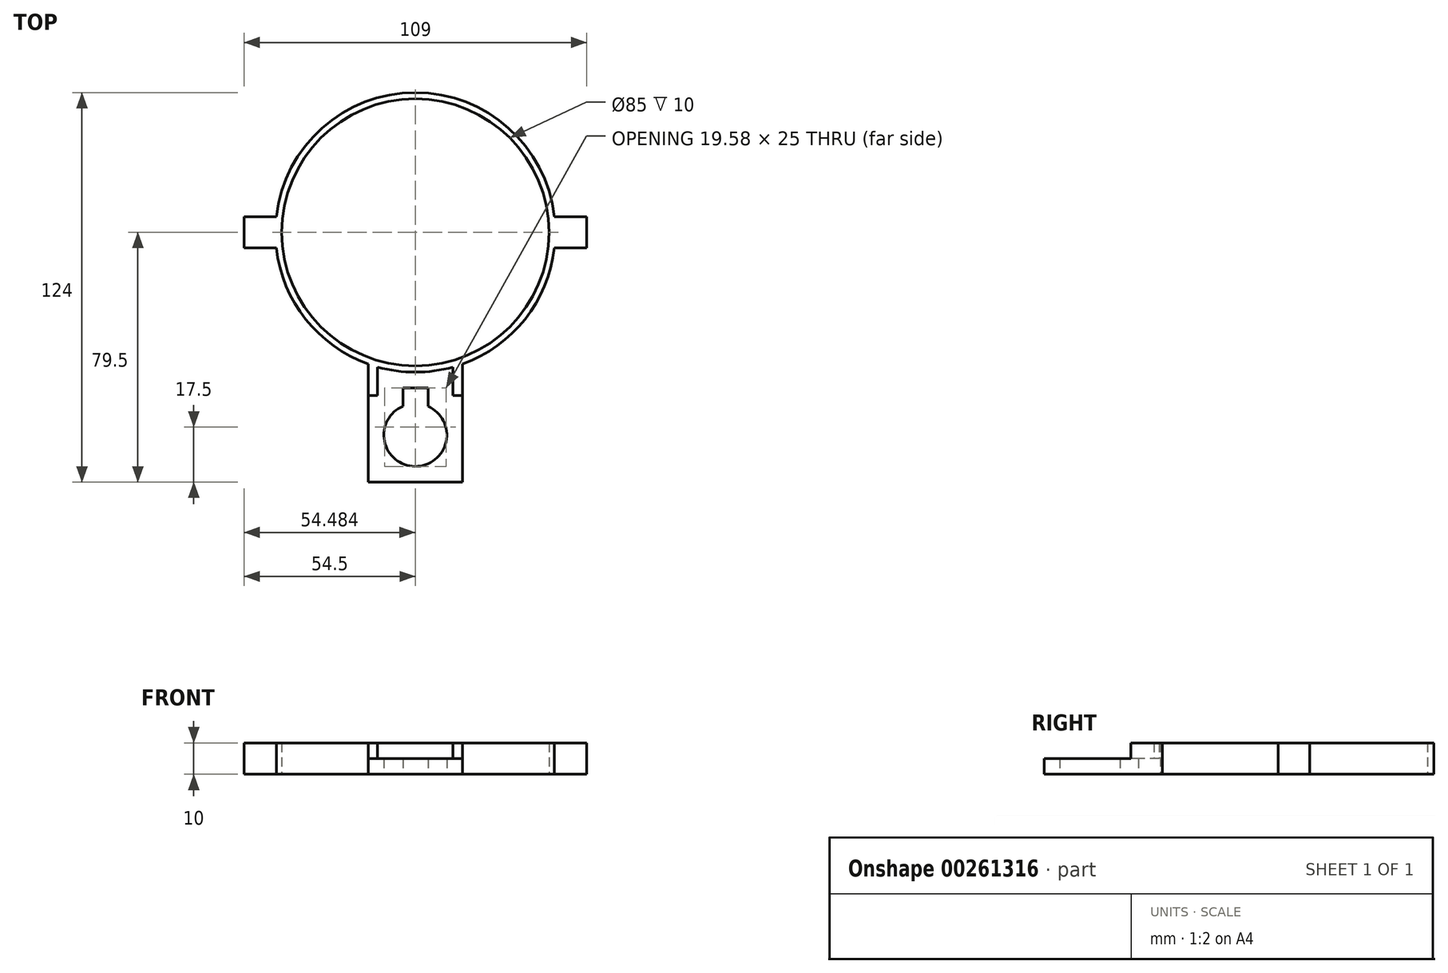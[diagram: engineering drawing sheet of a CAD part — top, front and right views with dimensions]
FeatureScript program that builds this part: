
annotation { "Feature Type Name" : "Feature", "Feature Type Description" : "" }
export const myFeature = defineFeature(function(context is Context, id is Id, definition is map)
    precondition{}
    {
        {
            var Q0;
            Q0=qCreatedBy(makeId("Top.planeOp"),FACE);
            var sketch = newSketch(context, id + "F0", { "sketchPlane" : qUnion([Q0])});
            skCircle(sketch, "E0", {"center": v(0, 0) * mm, "radius": 42.5 * mm});
            skCircle(sketch, "E1", {"center": v(0, 0) * mm, "radius": 44.5 * mm});
            skLineSegment(sketch, "E2.bottom", {"start": v(-54.5, 5) * mm, "end": v(-42.5, 5) * mm});
            skLineSegment(sketch, "E2.top", {"start": v(-54.5, -5) * mm, "end": v(-42.5, -5) * mm});
            skLineSegment(sketch, "E2.left", {"start": v(-54.5, 5) * mm, "end": v(-54.5, -5) * mm});
            skLineSegment(sketch, "E2.right", {"start": v(-42.5, 5) * mm, "end": v(-42.5, -5) * mm});
            skLineSegment(sketch, "E3.MirrorCS", {"start": v(54.5, 5) * mm, "end": v(54.5, -5) * mm});
            skLineSegment(sketch, "E4.MirrorCS", {"start": v(54.5, -5) * mm, "end": v(42.5, -5) * mm});
            skLineSegment(sketch, "E5.MirrorCS", {"start": v(54.5, 5) * mm, "end": v(42.5, 5) * mm});
            skLineSegment(sketch, "E6.MirrorCS", {"start": v(42.5, 5) * mm, "end": v(42.5, -5) * mm});
            skLineSegment(sketch, "E7.top", {"start": v(-15, -79.5) * mm, "end": v(15, -79.5) * mm});
            skLineSegment(sketch, "E7.left", {"start": v(-15, -41.9) * mm, "end": v(-15, -79.5) * mm});
            skLineSegment(sketch, "E7.right", {"start": v(15, -41.9) * mm, "end": v(15, -79.5) * mm});
            skCircle(sketch, "E8", {"center": v(0, -64.5) * mm, "radius": 10 * mm});
            skLineSegment(sketch, "E9.bottom", {"start": v(-3.93, -49.5) * mm, "end": v(4.07, -49.5) * mm});
            skLineSegment(sketch, "E9.top", {"start": v(-3.93, -64.5) * mm, "end": v(4.07, -64.5) * mm});
            skLineSegment(sketch, "E9.left", {"start": v(-3.93, -49.5) * mm, "end": v(-3.93, -64.5) * mm});
            skLineSegment(sketch, "E9.right", {"start": v(4.07, -49.5) * mm, "end": v(4.07, -64.5) * mm});
            skLineSegment(sketch, "E10.bottom", {"start": v(-15, -41.9) * mm, "end": v(-12, -41.9) * mm});
            skLineSegment(sketch, "E10.top", {"start": v(-15, -51.9) * mm, "end": v(-12, -51.9) * mm});
            skLineSegment(sketch, "E10.left", {"start": v(-15, -41.9) * mm, "end": v(-15, -51.9) * mm});
            skLineSegment(sketch, "E10.right", {"start": v(-12, -41.9) * mm, "end": v(-12, -51.9) * mm});
            skLineSegment(sketch, "E11.MirrorCS", {"start": v(15, -41.9) * mm, "end": v(12, -41.9) * mm});
            skLineSegment(sketch, "E12.MirrorCS", {"start": v(15, -51.9) * mm, "end": v(12, -51.9) * mm});
            skLineSegment(sketch, "E13.MirrorCS", {"start": v(15, -41.9) * mm, "end": v(15, -51.9) * mm});
            skLineSegment(sketch, "E14.MirrorCS", {"start": v(12, -41.9) * mm, "end": v(12, -51.9) * mm});
            skSolve(sketch);
        }
        {
            var Q0;
            {var subQ5=sQuery(id+"F0.wireOp",EDGE,"E2.left");Q0=makeQuery(id+"F0.imprint","IMPRINT",FACE,{"disambiguationData":[TD([[makeQuery(id+"F0.imprint","IMPRINT",EDGE,{"derivedFrom":subQ5}),1.0]])]});}
            var Q1;
            {var subQ5=sQuery(id+"F0.wireOp",EDGE,"E3.MirrorCS");Q1=makeQuery(id+"F0.imprint","IMPRINT",FACE,{"disambiguationData":[TD([[makeQuery(id+"F0.imprint","IMPRINT",EDGE,{"derivedFrom":subQ5}),-1.0]])]});}
            var Q2;
            {var subQ11=sQuery(id+"F0.wireOp",EDGE,"E10.bottom");Q2=makeQuery(id+"F0.imprint","IMPRINT",FACE,{"disambiguationData":[TD([[makeQuery(id+"F0.imprint","IMPRINT",EDGE,{"derivedFrom":subQ11}),1.0]])]});}
            var Q3;
            {var subQ1=sQuery(id+"F0.wireOp",EDGE,"E5.MirrorCS");var subQ4=sQuery(id+"F0.wireOp",EDGE,"E1");var subQ5=makeQuery(id+"F0.imprint","INTERSECT",VERTEX,{"derivedFrom":[subQ4,subQ1]});Q3=makeQuery(id+"F0.imprint","IMPRINT",FACE,{"disambiguationData":[TD([[makeQuery(id+"F0.imprint","IMPRINT",EDGE,{"disambiguationData":[TD([[subQ5,1.0]])],"derivedFrom":subQ4}),1.0]])]});}
            var Q4;
            {var subQ0=sQuery(id+"F0.wireOp",EDGE,"E2.right");var subQ3=sQuery(id+"F0.wireOp",EDGE,"E0");var subQ4=makeQuery(id+"F0.imprint","INTERSECT",VERTEX,{"derivedFrom":[subQ3,subQ0]});Q4=makeQuery(id+"F0.imprint","IMPRINT",FACE,{"disambiguationData":[TD([[makeQuery(id+"F0.imprint","IMPRINT",EDGE,{"disambiguationData":[TD([[subQ4,1.0]])],"derivedFrom":subQ3}),-1.0]])]});}
            var Q5;
            {var subQ1=sQuery(id+"F0.wireOp",EDGE,"E2.bottom");var subQ6=sQuery(id+"F0.wireOp",EDGE,"E1");var subQ8=makeQuery(id+"F0.imprint","INTERSECT",VERTEX,{"derivedFrom":[subQ6,subQ1]});Q5=makeQuery(id+"F0.imprint","IMPRINT",FACE,{"disambiguationData":[TD([[makeQuery(id+"F0.imprint","IMPRINT",EDGE,{"disambiguationData":[TD([[subQ8,-1.0]])],"derivedFrom":subQ6}),1.0]])]});}
            var Q6;
            {var subQ4=sQuery(id+"F0.wireOp",EDGE,"E12.MirrorCS");Q6=makeQuery(id+"F0.imprint","IMPRINT",FACE,{"disambiguationData":[TD([[makeQuery(id+"F0.imprint","IMPRINT",EDGE,{"derivedFrom":subQ4}),-1.0]])]});}
            var Q7;
            {var subQ4=sQuery(id+"F0.wireOp",EDGE,"E10.top");Q7=makeQuery(id+"F0.imprint","IMPRINT",FACE,{"disambiguationData":[TD([[makeQuery(id+"F0.imprint","IMPRINT",EDGE,{"derivedFrom":subQ4}),1.0]])]});}
            var Q8;
            {var subQ0=sQuery(id+"F0.wireOp",EDGE,"E10.bottom");Q8=makeQuery(id+"F0.imprint","IMPRINT",FACE,{"disambiguationData":[TD([[makeQuery(id+"F0.imprint","IMPRINT",EDGE,{"derivedFrom":subQ0}),-1.0]])]});}
            var Q9;
            {var subQ0=sQuery(id+"F0.wireOp",EDGE,"E11.MirrorCS");Q9=makeQuery(id+"F0.imprint","IMPRINT",FACE,{"disambiguationData":[TD([[makeQuery(id+"F0.imprint","IMPRINT",EDGE,{"derivedFrom":subQ0}),1.0]])]});}
            extrude(context, id + "F1", {"entities" : qUnion([Q0, Q1, Q2, Q3, Q4, Q5, Q6, Q7, Q8, Q9]), "depth" : 10 * mm});
        }
        {
            var Q0;
            Q0=makeQuery(id+"F0.imprint","IMPRINT",FACE,{"disambiguationData":[TD([[makeQuery(id+"F0.imprint","IMPRINT",EDGE,{"derivedFrom":sQuery(id+"F0.wireOp",EDGE,"E7.top")}),1.0]])]});
            extrude(context, id + "F2", {"entities" : qUnion([Q0]), "operationType" : NewBodyOperationType.ADD, "depth" : 5 * mm});
        }
    });
